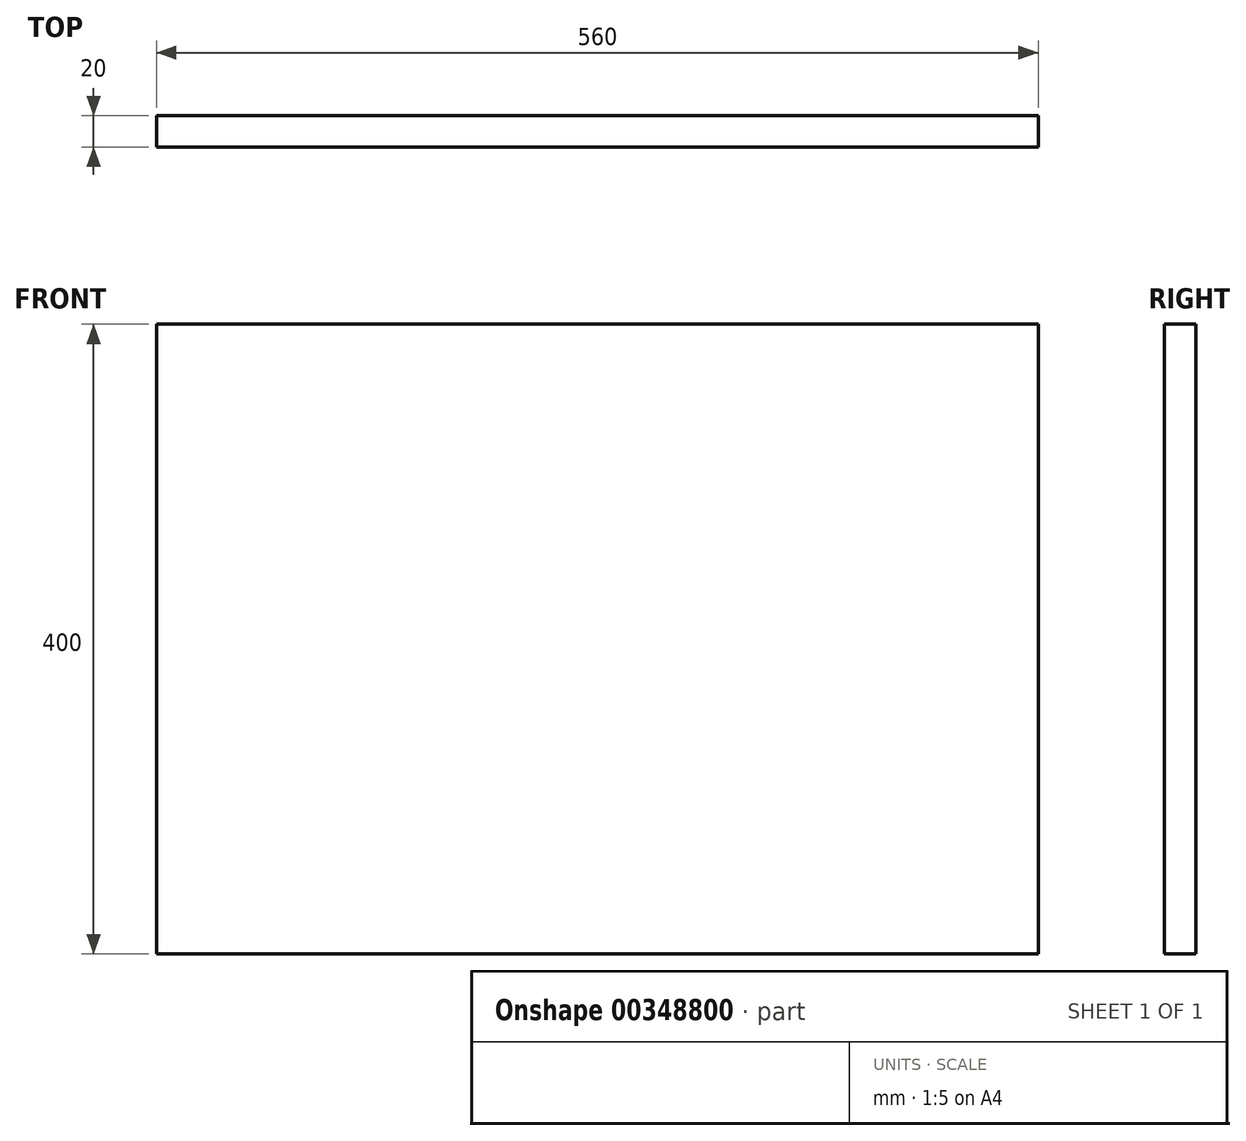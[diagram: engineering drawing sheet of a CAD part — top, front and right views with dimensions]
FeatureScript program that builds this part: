
annotation { "Feature Type Name" : "Feature", "Feature Type Description" : "" }
export const myFeature = defineFeature(function(context is Context, id is Id, definition is map)
    precondition{}
    {
        {
            var Q0;
            Q0=qCreatedBy(makeId("Front.planeOp"),FACE);
            var sketch = newSketch(context, id + "F0", { "sketchPlane" : qUnion([Q0])});
            skLineSegment(sketch, "E0.bottom", {"start": v(-560, -400) * mm, "end": v(0, -400) * mm});
            skLineSegment(sketch, "E0.top", {"start": v(-560, 0) * mm, "end": v(0, 0) * mm});
            skLineSegment(sketch, "E0.left", {"start": v(-560, -400) * mm, "end": v(-560, 0) * mm});
            skLineSegment(sketch, "E0.right", {"start": v(0, -400) * mm, "end": v(0, 0) * mm});
            skSolve(sketch);
        }
        {
            var Q0;
            Q0=qSketchRegion(id+"F0",true);
            extrude(context, id + "F1", {"entities" : qUnion([Q0]), "depth" : 20 * mm});
        }
    });
